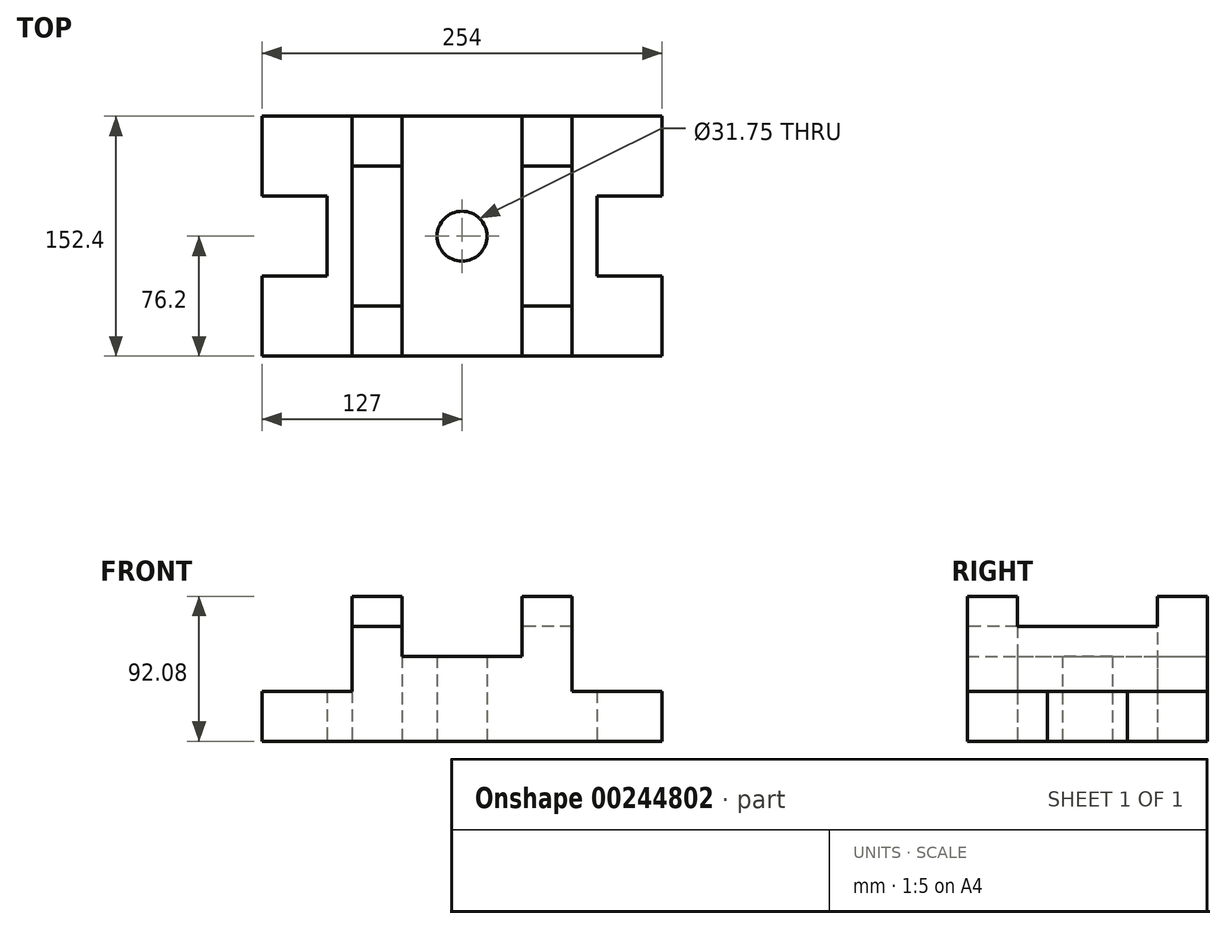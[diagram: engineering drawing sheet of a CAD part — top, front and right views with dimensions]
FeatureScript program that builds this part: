
annotation { "Feature Type Name" : "Feature", "Feature Type Description" : "" }
export const myFeature = defineFeature(function(context is Context, id is Id, definition is map)
    precondition{}
    {
        {
            var Q0;
            Q0=qCreatedBy(makeId("Top.planeOp"),FACE);
            var sketch = newSketch(context, id + "F0", { "sketchPlane" : qUnion([Q0])});
            skLineSegment(sketch, "E0", {"start": v(0, -76.2) * mm, "end": v(-127, -76.2) * mm});
            skLineSegment(sketch, "E1", {"start": v(-127, -76.2) * mm, "end": v(-127, -25.4) * mm});
            skLineSegment(sketch, "E2", {"start": v(-127, -25.4) * mm, "end": v(-85.72, -25.4) * mm});
            skLineSegment(sketch, "E3", {"start": v(-85.72, -25.4) * mm, "end": v(-85.72, 0) * mm});
            skLineSegment(sketch, "E4", {"start": v(-69.85, 0) * mm, "end": v(-69.85, -76.2) * mm});
            skLineSegment(sketch, "E5", {"start": v(-69.85, -76.2) * mm, "end": v(-38.1, -76.2) * mm});
            skLineSegment(sketch, "E6", {"start": v(-38.1, -76.2) * mm, "end": v(-38.1, 0) * mm});
            skCircle(sketch, "E7", {"center": v(0, 0) * mm, "radius": 15.88 * mm});
            skLineSegment(sketch, "E8", {"start": v(-69.85, -76.2) * mm, "end": v(-69.85, -44.45) * mm});
            skLineSegment(sketch, "E9", {"start": v(-69.85, -44.45) * mm, "end": v(-38.1, -44.45) * mm});
            skLineSegment(sketch, "E10.MirrorCS", {"start": v(0, 76.2) * mm, "end": v(-127, 76.2) * mm});
            skLineSegment(sketch, "E11.MirrorCS", {"start": v(-127, 25.4) * mm, "end": v(-85.72, 25.4) * mm});
            skLineSegment(sketch, "E12.MirrorCS", {"start": v(-127, 76.2) * mm, "end": v(-127, 25.4) * mm});
            skLineSegment(sketch, "E13.MirrorCS", {"start": v(-69.85, 44.45) * mm, "end": v(-38.1, 44.45) * mm});
            skLineSegment(sketch, "E14.MirrorCS", {"start": v(-69.85, 76.2) * mm, "end": v(-69.85, 44.45) * mm});
            skLineSegment(sketch, "E15.MirrorCS", {"start": v(-69.85, 0) * mm, "end": v(-69.85, 76.2) * mm});
            skLineSegment(sketch, "E16.MirrorCS", {"start": v(-69.85, 76.2) * mm, "end": v(-38.1, 76.2) * mm});
            skLineSegment(sketch, "E17.MirrorCS", {"start": v(-38.1, 76.2) * mm, "end": v(-38.1, 0) * mm});
            skLineSegment(sketch, "E18.MirrorCS", {"start": v(-85.72, 25.4) * mm, "end": v(-85.72, 0) * mm});
            skLineSegment(sketch, "E19.MirrorCS", {"start": v(69.85, 76.2) * mm, "end": v(69.85, 44.45) * mm});
            skLineSegment(sketch, "E20.MirrorCS", {"start": v(69.85, 76.2) * mm, "end": v(38.1, 76.2) * mm});
            skLineSegment(sketch, "E21.MirrorCS", {"start": v(85.72, 25.4) * mm, "end": v(85.72, 0) * mm});
            skLineSegment(sketch, "E22.MirrorCS", {"start": v(127, 76.2) * mm, "end": v(127, 25.4) * mm});
            skLineSegment(sketch, "E23.MirrorCS", {"start": v(127, 25.4) * mm, "end": v(85.72, 25.4) * mm});
            skLineSegment(sketch, "E24.MirrorCS", {"start": v(0, 76.2) * mm, "end": v(127, 76.2) * mm});
            skLineSegment(sketch, "E25.MirrorCS", {"start": v(69.85, -44.45) * mm, "end": v(38.1, -44.45) * mm});
            skLineSegment(sketch, "E26.MirrorCS", {"start": v(69.85, -76.2) * mm, "end": v(69.85, -44.45) * mm});
            skLineSegment(sketch, "E27.MirrorCS", {"start": v(38.1, -76.2) * mm, "end": v(38.1, 0) * mm});
            skLineSegment(sketch, "E28.MirrorCS", {"start": v(69.85, -76.2) * mm, "end": v(38.1, -76.2) * mm});
            skLineSegment(sketch, "E29.MirrorCS", {"start": v(69.85, 0) * mm, "end": v(69.85, -76.2) * mm});
            skLineSegment(sketch, "E30.MirrorCS", {"start": v(85.72, -25.4) * mm, "end": v(85.72, 0) * mm});
            skLineSegment(sketch, "E31.MirrorCS", {"start": v(127, -25.4) * mm, "end": v(85.72, -25.4) * mm});
            skLineSegment(sketch, "E32.MirrorCS", {"start": v(127, -76.2) * mm, "end": v(127, -25.4) * mm});
            skLineSegment(sketch, "E33.MirrorCS", {"start": v(69.85, 0) * mm, "end": v(69.85, 76.2) * mm});
            skLineSegment(sketch, "E34.MirrorCS", {"start": v(69.85, 44.45) * mm, "end": v(38.1, 44.45) * mm});
            skLineSegment(sketch, "E35.MirrorCS", {"start": v(38.1, 76.2) * mm, "end": v(38.1, 0) * mm});
            skLineSegment(sketch, "E36.MirrorCS", {"start": v(0, -76.2) * mm, "end": v(127, -76.2) * mm});
            skSolve(sketch);
        }
        {
            var Q0;
            Q0=makeQuery(id+"F0.imprint","IMPRINT",FACE,{"disambiguationData":[TD([[makeQuery(id+"F0.imprint","IMPRINT",EDGE,{"derivedFrom":sQuery(id+"F0.wireOp",EDGE,"E21.MirrorCS")}),-1.0]])]});
            var Q1;
            {var subQ7=sQuery(id+"F0.wireOp",EDGE,"E1");Q1=makeQuery(id+"F0.imprint","IMPRINT",FACE,{"disambiguationData":[TD([[makeQuery(id+"F0.imprint","IMPRINT",EDGE,{"derivedFrom":subQ7}),-1.0]])]});}
            extrude(context, id + "F1", {"entities" : qUnion([Q0, Q1]), "depth" : 31.75 * mm});
        }
        {
            var Q0;
            {var subQ0=sQuery(id+"F0.wireOp",EDGE,"E13.MirrorCS");Q0=makeQuery(id+"F0.imprint","IMPRINT",FACE,{"disambiguationData":[TD([[makeQuery(id+"F0.imprint","IMPRINT",EDGE,{"derivedFrom":subQ0}),1.0]])]});}
            var Q1;
            {var subQ5=sQuery(id+"F0.wireOp",EDGE,"E34.MirrorCS");Q1=makeQuery(id+"F0.imprint","IMPRINT",FACE,{"disambiguationData":[TD([[makeQuery(id+"F0.imprint","IMPRINT",EDGE,{"derivedFrom":subQ5}),-1.0]])]});}
            var Q2;
            {var subQ0=sQuery(id+"F0.wireOp",EDGE,"E25.MirrorCS");Q2=makeQuery(id+"F0.imprint","IMPRINT",FACE,{"disambiguationData":[TD([[makeQuery(id+"F0.imprint","IMPRINT",EDGE,{"derivedFrom":subQ0}),1.0]])]});}
            var Q3;
            {var subQ0=sQuery(id+"F0.wireOp",EDGE,"E5");Q3=makeQuery(id+"F0.imprint","IMPRINT",FACE,{"disambiguationData":[TD([[makeQuery(id+"F0.imprint","IMPRINT",EDGE,{"derivedFrom":subQ0}),1.0]])]});}
            extrude(context, id + "F2", {"entities" : qUnion([Q0, Q1, Q2, Q3]), "operationType" : NewBodyOperationType.ADD, "depth" : 92.07 * mm});
        }
        {
            var Q0;
            {var subQ5=sQuery(id+"F0.wireOp",EDGE,"E25.MirrorCS");Q0=makeQuery(id+"F0.imprint","IMPRINT",FACE,{"disambiguationData":[TD([[makeQuery(id+"F0.imprint","IMPRINT",EDGE,{"derivedFrom":subQ5}),-1.0]])]});}
            var Q1;
            {var subQ1=sQuery(id+"F0.wireOp",EDGE,"E4");Q1=makeQuery(id+"F0.imprint","IMPRINT",FACE,{"disambiguationData":[TD([[makeQuery(id+"F0.imprint","IMPRINT",EDGE,{"derivedFrom":subQ1}),1.0]])]});}
            extrude(context, id + "F3", {"entities" : qUnion([Q0, Q1]), "operationType" : NewBodyOperationType.ADD, "depth" : 73.02 * mm});
        }
        {
            var Q0;
            Q0=makeQuery(id+"F0.imprint","IMPRINT",FACE,{"disambiguationData":[TD([[makeQuery(id+"F0.imprint","IMPRINT",EDGE,{"derivedFrom":sQuery(id+"F0.wireOp",EDGE,"E7")}),-1.0]])]});
            extrude(context, id + "F4", {"entities" : qUnion([Q0]), "operationType" : NewBodyOperationType.ADD, "depth" : 53.97 * mm});
        }
    });
